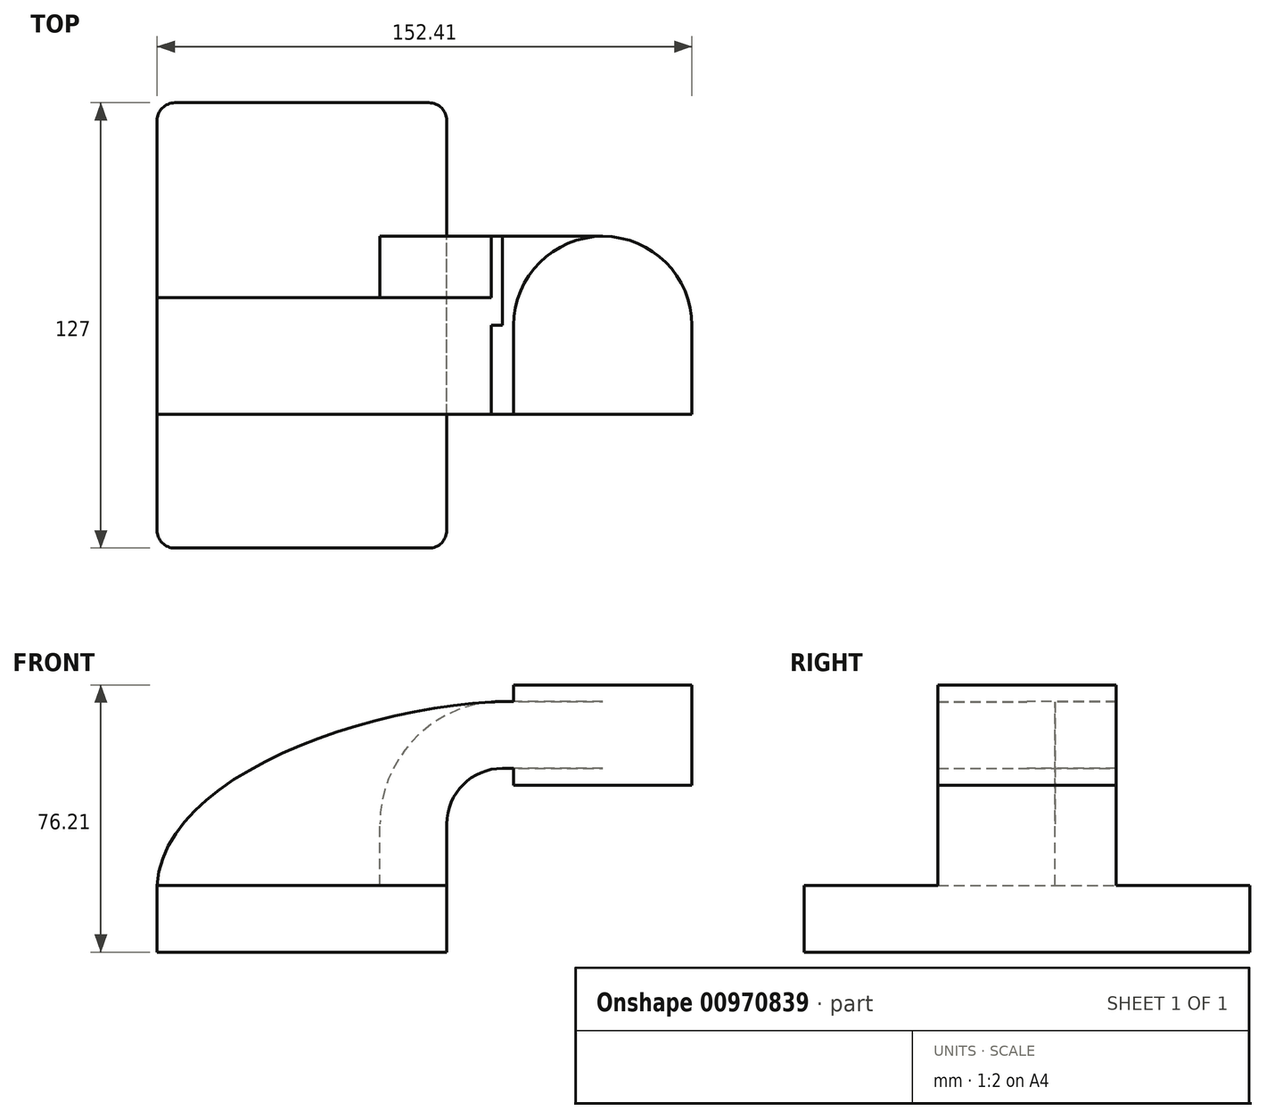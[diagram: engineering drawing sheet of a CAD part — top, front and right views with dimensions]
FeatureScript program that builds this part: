
annotation { "Feature Type Name" : "Feature", "Feature Type Description" : "" }
export const myFeature = defineFeature(function(context is Context, id is Id, definition is map)
    precondition{}
    {
        {
            var Q0;
            Q0=qCreatedBy(makeId("Front.planeOp"),FACE);
            var sketch = newSketch(context, id + "F0", { "sketchPlane" : qUnion([Q0])});
            skLineSegment(sketch, "E0.rect.bottom", {"start": v(-41.28, 9.52) * mm, "end": v(41.28, 9.52) * mm});
            skLineSegment(sketch, "E0.rect.top", {"start": v(-41.28, -9.52) * mm, "end": v(41.28, -9.52) * mm});
            skLineSegment(sketch, "E0.rect.left", {"start": v(-41.28, 9.52) * mm, "end": v(-41.28, -9.52) * mm});
            skLineSegment(sketch, "E0.rect.right", {"start": v(41.28, 9.52) * mm, "end": v(41.28, -9.52) * mm});
            skPoint(sketch, "E0.rect.middle", {"position": v(0, 0) * mm});
            skLineSegment(sketch, "E1", {"start": v(41.28, 9.52) * mm, "end": v(41.28, 27) * mm});
            skArc(sketch, "E2", {"start": v(41.28, 27) * mm, "mid": v(45.92, 38.23) * mm, "end": v(57.15, 42.88) * mm});
            skLineSegment(sketch, "E3", {"start": v(57.15, 42.88) * mm, "end": v(85.72, 42.88) * mm});
            skLineSegment(sketch, "E4.rect.bottom", {"start": v(60.32, 38.1) * mm, "end": v(111.12, 38.1) * mm});
            skLineSegment(sketch, "E4.rect.top", {"start": v(60.32, 66.68) * mm, "end": v(111.12, 66.68) * mm});
            skLineSegment(sketch, "E4.rect.left", {"start": v(60.32, 38.1) * mm, "end": v(60.32, 66.68) * mm});
            skLineSegment(sketch, "E4.rect.right", {"start": v(111.13, 38.1) * mm, "end": v(111.12, 66.68) * mm});
            skPoint(sketch, "E4.rect.middle", {"position": v(85.72, 52.39) * mm});
            skLineSegment(sketch, "E5.0", {"start": v(57.15, 61.93) * mm, "end": v(85.72, 61.93) * mm});
            skArc(sketch, "E5.1", {"start": v(22.23, 27) * mm, "mid": v(32.45, 51.7) * mm, "end": v(57.15, 61.93) * mm});
            skLineSegment(sketch, "E5.2", {"start": v(22.23, 9.52) * mm, "end": v(22.23, 27) * mm});
            skLineSegment(sketch, "E6", {"start": v(85.72, 38.1) * mm, "end": v(85.72, 66.68) * mm});
            skFitSpline(sketch, "E7", {"points": [v(-41.28, 9.53) * mm, v(57.15, 61.93) * mm], "startDerivative": vector(5.2, 92.34) * mm, "endDerivative": vector(120.92, 4.22) * mm});
            skSolve(sketch);
        }
        {
            var Q0;
            Q0=makeQuery(id+"F0.imprint","IMPRINT",FACE,{"disambiguationData":[TD([[makeQuery(id+"F0.imprint","IMPRINT",EDGE,{"derivedFrom":sQuery(id+"F0.wireOp",EDGE,"E0.rect.top")}),1.0]])]});
            extrude(context, id + "F1", {"entities" : qUnion([Q0]), "endBound" : BoundingType.SYMMETRIC, "depth" : 127 * mm});
        }
        {
            var Q0;
            {var subQ9=sQuery(id+"F0.wireOp",EDGE,"E1");Q0=makeQuery(id+"F0.imprint","IMPRINT",FACE,{"disambiguationData":[TD([[makeQuery(id+"F0.imprint","IMPRINT",EDGE,{"derivedFrom":subQ9}),1.0]])]});}
            var Q1;
            {var subQ0=sQuery(id+"F0.wireOp",EDGE,"E6");var subQ1=sQuery(id+"F0.wireOp",EDGE,"E3");var subQ2=makeQuery(id+"F0.imprint","INTERSECT",VERTEX,{"derivedFrom":[subQ1,subQ0]});Q1=makeQuery(id+"F0.imprint","IMPRINT",FACE,{"disambiguationData":[TD([[makeQuery(id+"F0.imprint","IMPRINT",EDGE,{"disambiguationData":[TD([[subQ2,1.0]])],"derivedFrom":subQ1}),1.0]])]});}
            extrude(context, id + "F2", {"entities" : qUnion([Q0, Q1]), "operationType" : NewBodyOperationType.ADD, "endBound" : BoundingType.SYMMETRIC, "depth" : 50.8 * mm});
        }
        {
            var Q0;
            {var subQ3=sQuery(id+"F0.wireOp",EDGE,"E5.2");Q0=makeQuery(id+"F0.imprint","IMPRINT",FACE,{"disambiguationData":[TD([[makeQuery(id+"F0.imprint","IMPRINT",EDGE,{"derivedFrom":subQ3}),1.0]])]});}
            extrude(context, id + "F3", {"entities" : qUnion([Q0]), "operationType" : NewBodyOperationType.ADD, "endBound" : BoundingType.SYMMETRIC, "depth" : 15.88 * mm});
        }
        {
            var Q0;
            {var subQ5=sQuery(id+"F0.wireOp",EDGE,"E4.rect.right");Q0=makeQuery(id+"F0.imprint","IMPRINT",FACE,{"disambiguationData":[TD([[makeQuery(id+"F0.imprint","IMPRINT",EDGE,{"derivedFrom":subQ5}),1.0]])]});}
            var Q1;
            Q1=sQuery(id+"F0.wireOp",EDGE,"E6");
            revolve(context, id + "F4", {"operationType" : NewBodyOperationType.ADD, "entities" : qUnion([Q0]), "axis" : qUnion([Q1]), "revolveType" : RevolveType.FULL});
        }
        {
            var Q0;
            Q0=makeQuery(id+"F1.opExtrude","CAP_EDGE",EDGE,{"disambiguationData":[OSD([sQuery(id+"F0.wireOp",EDGE,"E0.rect.right")])],"isStart":false});
            var Q1;
            Q1=makeQuery(id+"F1.opExtrude","CAP_EDGE",EDGE,{"disambiguationData":[OSD([sQuery(id+"F0.wireOp",EDGE,"E0.rect.left")])],"isStart":false});
            var Q2;
            Q2=makeQuery(id+"F1.opExtrude","CAP_EDGE",EDGE,{"disambiguationData":[OSD([sQuery(id+"F0.wireOp",EDGE,"E0.rect.right")])],"isStart":true});
            var Q3;
            Q3=makeQuery(id+"F1.opExtrude","CAP_EDGE",EDGE,{"disambiguationData":[OSD([sQuery(id+"F0.wireOp",EDGE,"E0.rect.left")])],"isStart":true});
            fillet(context, id + "F5", {"entities" : qUnion([Q0, Q1, Q2, Q3]), "radius" : 5.08 * mm, "tangentPropagation" : true, "allowEdgeOverflow" : false});
        }
        {
            var Q0;
            Q0 = qSketchRegion(id + "F0", true);
            extrude(context, id + "F6", {"entities" : qUnion([Q0]), "operationType" : NewBodyOperationType.ADD, "depth" : 25.4 * mm, "offsetDistance" : 25.4 * mm});
        }
    });
